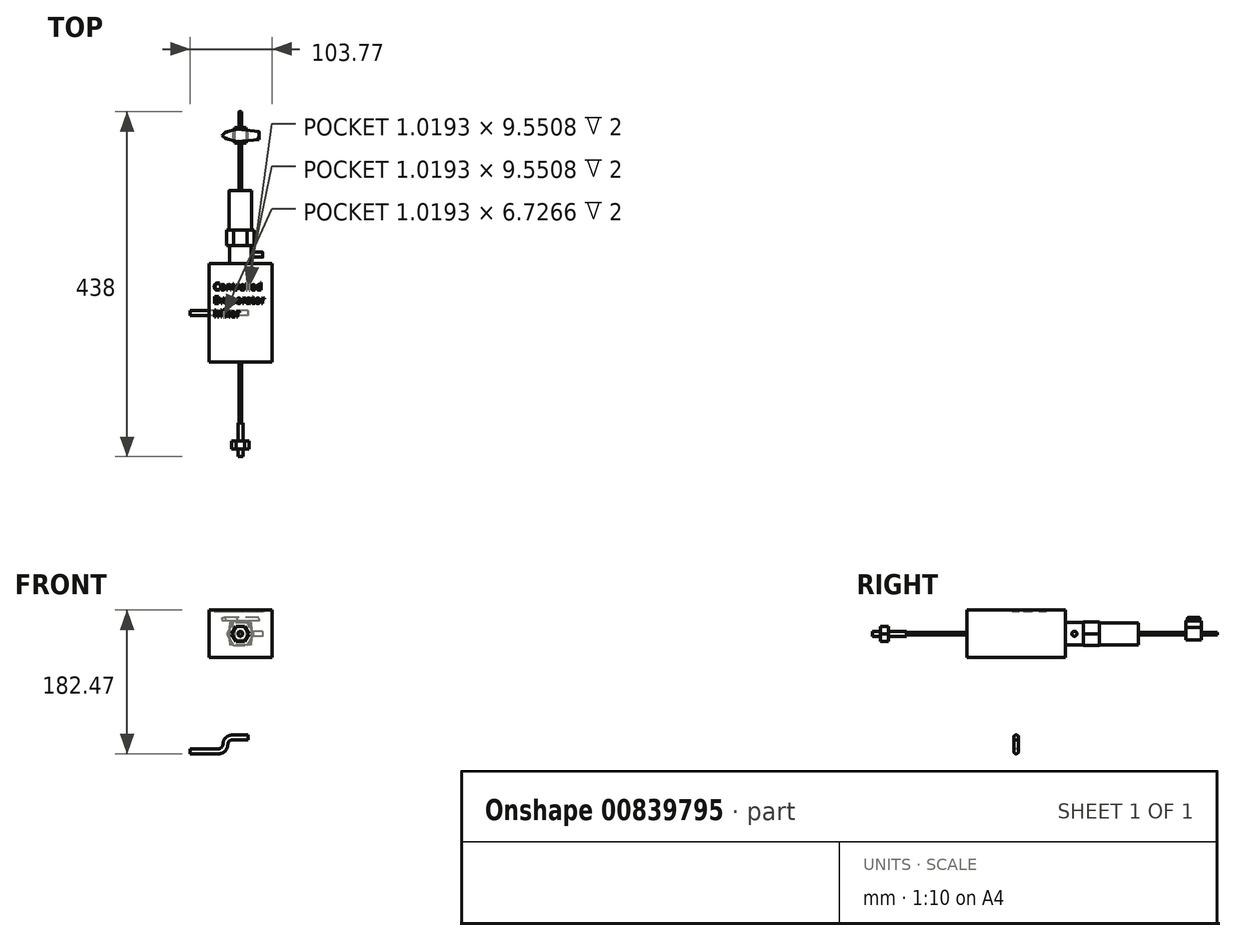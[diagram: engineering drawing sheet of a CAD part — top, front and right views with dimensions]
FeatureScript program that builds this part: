
annotation { "Feature Type Name" : "Feature", "Feature Type Description" : "" }
export const myFeature = defineFeature(function(context is Context, id is Id, definition is map)
    precondition{}
    {
        {
            var Q0;
            Q0=qCreatedBy(makeId("Top.planeOp"),FACE);
            var sketch = newSketch(context, id + "F0", { "sketchPlane" : qUnion([Q0])});
            skLineSegment(sketch, "E0.bottom", {"start": v(-40, 62.5) * mm, "end": v(40, 62.5) * mm});
            skLineSegment(sketch, "E0.top", {"start": v(-40, -62.5) * mm, "end": v(40, -62.5) * mm});
            skLineSegment(sketch, "E0.left", {"start": v(-40, 62.5) * mm, "end": v(-40, -62.5) * mm});
            skLineSegment(sketch, "E0.right", {"start": v(40, 62.5) * mm, "end": v(40, -62.5) * mm});
            skPoint(sketch, "E0.middle", {"position": v(0, 0) * mm});
            skSolve(sketch);
        }
        {
            var Q0;
            Q0 = qSketchRegion(id + "F0", true);
            extrude(context, id + "F1", {"entities" : qUnion([Q0]), "depth" : 60 * mm, "offsetDistance" : 25 * mm});
        }
        {
            var Q0;
            Q0=makeQuery(id+"F1.opExtrude","SWEPT_FACE",FACE,{"disambiguationData":[OSD([sQuery(id+"F0.wireOp",EDGE,"E0.bottom")])]});
            var sketch = newSketch(context, id + "F2", { "sketchPlane" : qUnion([Q0])});
            skLineSegment(sketch, "E1", {"start": v(-40, 30) * mm, "end": v(40, 30) * mm});
            skLineSegment(sketch, "E2.bottom", {"start": v(-13.5, 44.5) * mm, "end": v(13.5, 44.5) * mm});
            skLineSegment(sketch, "E2.top", {"start": v(-13.5, 15.5) * mm, "end": v(13.5, 15.5) * mm});
            skLineSegment(sketch, "E2.left", {"start": v(-13.5, 44.5) * mm, "end": v(-13.5, 15.5) * mm});
            skLineSegment(sketch, "E2.right", {"start": v(13.5, 44.5) * mm, "end": v(13.5, 15.5) * mm});
            skPoint(sketch, "E2.middle", {"position": v(0, 30) * mm});
            skSolve(sketch);
        }
        {
            var Q0;
            Q0 = qSketchRegion(id + "F2", true);
            extrude(context, id + "F3", {"entities" : qUnion([Q0]), "operationType" : NewBodyOperationType.ADD, "depth" : 23 * mm, "offsetDistance" : 25 * mm});
        }
        {
            var Q0;
            Q0=makeQuery(id+"F3.opExtrude","CAP_FACE",FACE,{"disambiguationData":[OSD([sQuery(id+"F2.wireOp",EDGE,"E2.bottom"),sQuery(id+"F2.wireOp",EDGE,"E2.top"),sQuery(id+"F2.wireOp",EDGE,"E2.left"),sQuery(id+"F2.wireOp",EDGE,"E2.right")])],"isStart":false});
            var sketch = newSketch(context, id + "F4", { "sketchPlane" : qUnion([Q0])});
            skLineSegment(sketch, "E3", {"start": v(-13.5, 30) * mm, "end": v(13.5, 30) * mm, "construction": true});
            skPoint(sketch, "E4.cCircle.perimeterSnap0", {"position": v(0, 44.5) * mm});
            skPoint(sketch, "E4.0.startSnap0", {"position": v(0, 44.5) * mm});
            skCircle(sketch, "E5.cCircle", {"center": v(0, 30) * mm, "radius": 15 * mm, "construction": true});
            skLineSegment(sketch, "E5.0", {"start": v(-8.66, 45) * mm, "end": v(8.66, 45) * mm});
            skLineSegment(sketch, "E5.1", {"start": v(8.66, 45) * mm, "end": v(17.32, 30) * mm});
            skLineSegment(sketch, "E5.2", {"start": v(17.32, 30) * mm, "end": v(8.66, 15) * mm});
            skLineSegment(sketch, "E5.3", {"start": v(8.66, 15) * mm, "end": v(-8.66, 15) * mm});
            skLineSegment(sketch, "E5.4", {"start": v(-8.66, 15) * mm, "end": v(-17.32, 30) * mm});
            skLineSegment(sketch, "E5.5", {"start": v(-17.32, 30) * mm, "end": v(-8.66, 45) * mm});
            skPoint(sketch, "E5.0.midPoint", {"position": v(0, 45) * mm});
            skSolve(sketch);
        }
        {
            var Q0;
            Q0 = qSketchRegion(id + "F4", true);
            extrude(context, id + "F5", {"entities" : qUnion([Q0]), "operationType" : NewBodyOperationType.ADD, "depth" : 20 * mm, "offsetDistance" : 25 * mm});
        }
        {
            var Q0;
            Q0=makeQuery(id+"F5.opExtrude","CAP_FACE",FACE,{"disambiguationData":[OSD([sQuery(id+"F4.wireOp",EDGE,"E5.0"),sQuery(id+"F4.wireOp",EDGE,"E5.1"),sQuery(id+"F4.wireOp",EDGE,"E5.2"),sQuery(id+"F4.wireOp",EDGE,"E5.3"),sQuery(id+"F4.wireOp",EDGE,"E5.4"),sQuery(id+"F4.wireOp",EDGE,"E5.5")])],"isStart":false});
            var sketch = newSketch(context, id + "F6", { "sketchPlane" : qUnion([Q0])});
            skLineSegment(sketch, "E6", {"start": v(-17.32, 30) * mm, "end": v(17.32, 30) * mm, "construction": true});
            skLineSegment(sketch, "E7.bottom", {"start": v(-14, 44) * mm, "end": v(14, 44) * mm});
            skLineSegment(sketch, "E7.top", {"start": v(-14, 16) * mm, "end": v(14, 16) * mm});
            skLineSegment(sketch, "E7.left", {"start": v(-14, 44) * mm, "end": v(-14, 16) * mm});
            skLineSegment(sketch, "E7.right", {"start": v(14, 44) * mm, "end": v(14, 16) * mm});
            skPoint(sketch, "E7.middle", {"position": v(0, 30) * mm});
            skSolve(sketch);
        }
        {
            var Q0;
            Q0 = qSketchRegion(id + "F6", true);
            extrude(context, id + "F7", {"entities" : qUnion([Q0]), "operationType" : NewBodyOperationType.ADD, "depth" : 50 * mm, "offsetDistance" : 25 * mm});
        }
        {
            var Q0;
            Q0=makeQuery(id+"F7.opExtrude","SWEPT_EDGE",EDGE,{"disambiguationData":[OSD([sQuery(id+"F6.wireOp",EDGE,"E7.bottom"),sQuery(id+"F6.wireOp",EDGE,"E7.left")])]});
            var Q1;
            Q1=makeQuery(id+"F7.opExtrude","SWEPT_EDGE",EDGE,{"disambiguationData":[OSD([sQuery(id+"F6.wireOp",EDGE,"E7.bottom"),sQuery(id+"F6.wireOp",EDGE,"E7.right")])]});
            var Q2;
            Q2=makeQuery(id+"F7.opExtrude","SWEPT_EDGE",EDGE,{"disambiguationData":[OSD([sQuery(id+"F6.wireOp",EDGE,"E7.top"),sQuery(id+"F6.wireOp",EDGE,"E7.right")])]});
            var Q3;
            Q3=makeQuery(id+"F7.opExtrude","SWEPT_EDGE",EDGE,{"disambiguationData":[OSD([sQuery(id+"F6.wireOp",EDGE,"E7.top"),sQuery(id+"F6.wireOp",EDGE,"E7.left")])]});
            fillet(context, id + "F8", {"entities" : qUnion([Q0, Q1, Q2, Q3]), "radius" : 5 * mm, "tangentPropagation" : true, "allowEdgeOverflow" : false});
        }
        {
            var Q0;
            Q0=makeQuery(id+"F7.opExtrude","CAP_FACE",FACE,{"disambiguationData":[OSD([sQuery(id+"F6.wireOp",EDGE,"E7.bottom"),sQuery(id+"F6.wireOp",EDGE,"E7.top"),sQuery(id+"F6.wireOp",EDGE,"E7.left"),sQuery(id+"F6.wireOp",EDGE,"E7.right")])],"isStart":false});
            var sketch = newSketch(context, id + "F9", { "sketchPlane" : qUnion([Q0])});
            skLineSegment(sketch, "E8", {"start": v(-14, 30) * mm, "end": v(14, 30) * mm, "construction": true});
            skCircle(sketch, "E9", {"center": v(0, 30) * mm, "radius": 1.59 * mm});
            skSolve(sketch);
        }
        {
            var Q0;
            Q0 = qSketchRegion(id + "F9", true);
            extrude(context, id + "F10", {"entities" : qUnion([Q0]), "operationType" : NewBodyOperationType.ADD, "depth" : 60 * mm, "offsetDistance" : 25 * mm});
        }
        {
            var Q0;
            Q0=makeQuery(id+"F10.opExtrude","CAP_FACE",FACE,{"disambiguationData":[OSD([sQuery(id+"F9.wireOp",EDGE,"E9")])],"isStart":false});
            var sketch = newSketch(context, id + "F11", { "sketchPlane" : qUnion([Q0])});
            skLineSegment(sketch, "E10.bottom", {"start": v(-7.5, 38) * mm, "end": v(7.5, 38) * mm});
            skLineSegment(sketch, "E10.top", {"start": v(-7.5, 22) * mm, "end": v(7.5, 22) * mm});
            skLineSegment(sketch, "E10.left", {"start": v(-7.5, 38) * mm, "end": v(-7.5, 22) * mm});
            skLineSegment(sketch, "E10.right", {"start": v(7.5, 38) * mm, "end": v(7.5, 22) * mm});
            skPoint(sketch, "E10.middle", {"position": v(0, 30) * mm});
            skSolve(sketch);
        }
        {
            var Q0;
            Q0 = qSketchRegion(id + "F11", true);
            extrude(context, id + "F12", {"entities" : qUnion([Q0]), "operationType" : NewBodyOperationType.ADD, "depth" : 20 * mm, "offsetDistance" : 25 * mm});
        }
        {
            var Q0;
            Q0=makeQuery(id+"F12.opExtrude","CAP_FACE",FACE,{"disambiguationData":[OSD([sQuery(id+"F11.wireOp",EDGE,"E10.bottom"),sQuery(id+"F11.wireOp",EDGE,"E10.top"),sQuery(id+"F11.wireOp",EDGE,"E10.left"),sQuery(id+"F11.wireOp",EDGE,"E10.right")])],"isStart":false});
            var sketch = newSketch(context, id + "F13", { "sketchPlane" : qUnion([Q0])});
            skLineSegment(sketch, "E11", {"start": v(-7.5, 30) * mm, "end": v(7.5, 30) * mm, "construction": true});
            skCircle(sketch, "E12", {"center": v(0, 30) * mm, "radius": 1.59 * mm});
            skSolve(sketch);
        }
        {
            var Q0;
            Q0=makeQuery(id+"F13.imprint","IMPRINT",FACE,{"disambiguationData":[TD([[makeQuery(id+"F13.imprint","IMPRINT",EDGE,{"derivedFrom":sQuery(id+"F13.wireOp",EDGE,"E12")}),1.0]])]});
            var Q1;
            Q1 = qConstructionFilter(qBodyType(qCreatedBy(id + "F13" ,EDGE), BodyType.WIRE), ConstructionObject.NO);
            extrude(context, id + "F14", {"entities" : qUnion([Q0]), "operationType" : NewBodyOperationType.ADD, "surfaceEntities" : qUnion([Q1]), "depth" : 20 * mm, "offsetDistance" : 25 * mm});
        }
        {
            var Q0;
            Q0=makeQuery(id+"F12.opExtrude","SWEPT_FACE",FACE,{"disambiguationData":[OSD([sQuery(id+"F11.wireOp",EDGE,"E10.bottom")])]});
            var sketch = newSketch(context, id + "F15", { "sketchPlane" : qUnion([Q0])});
            skLineSegment(sketch, "E13", {"start": v(-7.5, 225.5) * mm, "end": v(7.5, 225.5) * mm, "construction": true});
            skCircle(sketch, "E14", {"center": v(0, 225.5) * mm, "radius": 10 * mm});
            skSolve(sketch);
        }
        {
            var Q0;
            Q0 = qSketchRegion(id + "F15", true);
            extrude(context, id + "F16", {"entities" : qUnion([Q0]), "operationType" : NewBodyOperationType.ADD, "depth" : 8 * mm, "offsetDistance" : 25 * mm});
        }
        {
            var Q0;
            Q0=makeQuery(id+"F16.opExtrude","CAP_FACE",FACE,{"disambiguationData":[OSD([sQuery(id+"F15.wireOp",EDGE,"E14")])],"isStart":false});
            var sketch = newSketch(context, id + "F17", { "sketchPlane" : qUnion([Q0])});
            skLineSegment(sketch, "E15.bottom", {"start": v(-23.5, 233.5) * mm, "end": v(23.5, 233.5) * mm, "construction": true});
            skLineSegment(sketch, "E15.top", {"start": v(-23.5, 217.5) * mm, "end": v(23.5, 217.5) * mm, "construction": true});
            skLineSegment(sketch, "E15.left", {"start": v(-23.5, 233.5) * mm, "end": v(-23.5, 217.5) * mm, "construction": true});
            skLineSegment(sketch, "E15.right", {"start": v(23.5, 233.5) * mm, "end": v(23.5, 217.5) * mm, "construction": true});
            skPoint(sketch, "E15.middle", {"position": v(0, 225.5) * mm});
            skPoint(sketch, "E16", {"position": v(23.5, 230.5) * mm});
            skPoint(sketch, "E17", {"position": v(23.5, 220.5) * mm});
            skLineSegment(sketch, "E18", {"start": v(23.5, 230.5) * mm, "end": v(-4.34, 233.5) * mm});
            skLineSegment(sketch, "E19", {"start": v(-4.34, 233.5) * mm, "end": v(-18.8, 229.5) * mm});
            skLineSegment(sketch, "E20", {"start": v(-18.8, 229.5) * mm, "end": v(-23.5, 225.5) * mm});
            skLineSegment(sketch, "E21", {"start": v(-23.5, 225.5) * mm, "end": v(23.5, 225.5) * mm, "construction": true});
            skLineSegment(sketch, "E22.MirrorCS", {"start": v(-18.8, 221.5) * mm, "end": v(-23.5, 225.5) * mm});
            skLineSegment(sketch, "E23.MirrorCS", {"start": v(-4.34, 217.5) * mm, "end": v(-18.8, 221.5) * mm});
            skLineSegment(sketch, "E24.MirrorCS", {"start": v(23.5, 220.5) * mm, "end": v(-4.34, 217.5) * mm});
            skLineSegment(sketch, "E25", {"start": v(23.5, 230.5) * mm, "end": v(23.5, 220.5) * mm});
            skSolve(sketch);
        }
        {
            var Q0;
            {var subQ4=sQuery(id+"F17.wireOp",EDGE,"E20");Q0=makeQuery(id+"F17.imprint","IMPRINT",FACE,{"disambiguationData":[TD([[makeQuery(id+"F17.imprint","IMPRINT",EDGE,{"derivedFrom":subQ4}),1.0]])]});}
            var Q1;
            {var subQ5=sQuery(id+"F17.wireOp",EDGE,"E19");var subQ6=sQuery(id+"F17.wireOp",EDGE,"E18");var subQ7=makeQuery(id+"F17.imprint","INTERSECT",VERTEX,{"derivedFrom":[subQ6,subQ5]});Q1=makeQuery(id+"F17.imprint","IMPRINT",FACE,{"disambiguationData":[TD([[makeQuery(id+"F17.imprint","IMPRINT",EDGE,{"disambiguationData":[TD([[subQ7,1.0]])],"derivedFrom":subQ6}),1.0]])]});}
            var Q2;
            {var subQ0=sQuery(id+"F17.wireOp",EDGE,"E25");Q2=makeQuery(id+"F17.imprint","IMPRINT",FACE,{"disambiguationData":[TD([[makeQuery(id+"F17.imprint","IMPRINT",EDGE,{"derivedFrom":subQ0}),-1.0]])]});}
            extrude(context, id + "F18", {"entities" : qUnion([Q0, Q1, Q2]), "operationType" : NewBodyOperationType.ADD, "depth" : 5 * mm, "offsetDistance" : 25 * mm});
        }
        {
            var Q0;
            Q0=makeQuery(id+"F18.opExtrude","CAP_EDGE",EDGE,{"disambiguationData":[OSD([sQuery(id+"F17.wireOp",EDGE,"E18")])],"isStart":false});
            var Q1;
            Q1=makeQuery(id+"F18.opExtrude","CAP_EDGE",EDGE,{"disambiguationData":[OSD([sQuery(id+"F17.wireOp",EDGE,"E19")])],"isStart":false});
            var Q2;
            Q2=makeQuery(id+"F18.opExtrude","CAP_EDGE",EDGE,{"disambiguationData":[OSD([sQuery(id+"F17.wireOp",EDGE,"E20")])],"isStart":false});
            var Q3;
            Q3=makeQuery(id+"F18.opExtrude","CAP_EDGE",EDGE,{"disambiguationData":[OSD([sQuery(id+"F17.wireOp",EDGE,"E22.MirrorCS")])],"isStart":false});
            var Q4;
            Q4=makeQuery(id+"F18.opExtrude","CAP_EDGE",EDGE,{"disambiguationData":[OSD([sQuery(id+"F17.wireOp",EDGE,"E23.MirrorCS")])],"isStart":false});
            var Q5;
            Q5=makeQuery(id+"F18.opExtrude","CAP_EDGE",EDGE,{"disambiguationData":[OSD([sQuery(id+"F17.wireOp",EDGE,"E24.MirrorCS")])],"isStart":false});
            var Q6;
            Q6=makeQuery(id+"F18.opExtrude","CAP_EDGE",EDGE,{"disambiguationData":[OSD([sQuery(id+"F17.wireOp",EDGE,"E25")])],"isStart":false});
            fillet(context, id + "F19", {"entities" : qUnion([Q0, Q1, Q2, Q3, Q4, Q5, Q6]), "radius" : 2 * mm, "tangentPropagation" : true, "allowEdgeOverflow" : false});
        }
        {
            var Q0;
            Q0=makeQuery(id+"F1.opExtrude","SWEPT_FACE",FACE,{"disambiguationData":[OSD([sQuery(id+"F0.wireOp",EDGE,"E0.top")])]});
            var sketch = newSketch(context, id + "F20", { "sketchPlane" : qUnion([Q0])});
            skLineSegment(sketch, "E26", {"start": v(-40, 30) * mm, "end": v(40, 30) * mm, "construction": true});
            skCircle(sketch, "E27", {"center": v(0, 30) * mm, "radius": 1.59 * mm});
            skPoint(sketch, "E28", {"position": v(0, 31.59) * mm});
            skSolve(sketch);
        }
        {
            var Q0;
            Q0 = qSketchRegion(id + "F20", true);
            extrude(context, id + "F21", {"entities" : qUnion([Q0]), "operationType" : NewBodyOperationType.ADD, "depth" : 77 * mm, "offsetDistance" : 25 * mm});
        }
        {
            var Q0;
            Q0=makeQuery(id+"F21.opExtrude","CAP_FACE",FACE,{"disambiguationData":[OSD([sQuery(id+"F20.wireOp",EDGE,"E27")])],"isStart":false});
            var sketch = newSketch(context, id + "F22", { "sketchPlane" : qUnion([Q0])});
            skCircle(sketch, "E29", {"center": v(0, 30) * mm, "radius": 3.18 * mm});
            skSolve(sketch);
        }
        {
            var Q0;
            Q0 = qSketchRegion(id + "F22", true);
            extrude(context, id + "F23", {"entities" : qUnion([Q0]), "operationType" : NewBodyOperationType.ADD, "depth" : 23 * mm, "offsetDistance" : 25 * mm});
        }
        {
            var Q0;
            Q0=makeQuery(id+"F23.opExtrude","CAP_FACE",FACE,{"disambiguationData":[OSD([sQuery(id+"F22.wireOp",EDGE,"E29")])],"isStart":false});
            var sketch = newSketch(context, id + "F24", { "sketchPlane" : qUnion([Q0])});
            skCircle(sketch, "E30.cCircle", {"center": v(0, 30) * mm, "radius": 9.5 * mm, "construction": true});
            skLineSegment(sketch, "E30.0", {"start": v(-5.48, 39.5) * mm, "end": v(5.48, 39.5) * mm});
            skLineSegment(sketch, "E30.1", {"start": v(5.48, 39.5) * mm, "end": v(10.97, 30) * mm});
            skLineSegment(sketch, "E30.2", {"start": v(10.97, 30) * mm, "end": v(5.48, 20.5) * mm});
            skLineSegment(sketch, "E30.3", {"start": v(5.48, 20.5) * mm, "end": v(-5.48, 20.5) * mm});
            skLineSegment(sketch, "E30.4", {"start": v(-5.48, 20.5) * mm, "end": v(-10.97, 30) * mm});
            skLineSegment(sketch, "E30.5", {"start": v(-10.97, 30) * mm, "end": v(-5.48, 39.5) * mm});
            skPoint(sketch, "E30.0.midPoint", {"position": v(0, 39.5) * mm});
            skSolve(sketch);
        }
        {
            var Q0;
            Q0 = qSketchRegion(id + "F24", true);
            extrude(context, id + "F25", {"entities" : qUnion([Q0]), "operationType" : NewBodyOperationType.ADD, "depth" : 10 * mm, "offsetDistance" : 25 * mm});
        }
        {
            var Q0;
            Q0=makeQuery(id+"F25.opExtrude","CAP_FACE",FACE,{"disambiguationData":[OSD([sQuery(id+"F24.wireOp",EDGE,"E30.0"),sQuery(id+"F24.wireOp",EDGE,"E30.1"),sQuery(id+"F24.wireOp",EDGE,"E30.2"),sQuery(id+"F24.wireOp",EDGE,"E30.3"),sQuery(id+"F24.wireOp",EDGE,"E30.4"),sQuery(id+"F24.wireOp",EDGE,"E30.5")])],"isStart":false});
            var sketch = newSketch(context, id + "F26", { "sketchPlane" : qUnion([Q0])});
            skCircle(sketch, "E31", {"center": v(0, 30) * mm, "radius": 3.17 * mm});
            skLineSegment(sketch, "E32", {"start": v(-10.97, 30) * mm, "end": v(10.97, 30) * mm, "construction": true});
            skSolve(sketch);
        }
        {
            var Q0;
            Q0 = qSketchRegion(id + "F26", true);
            extrude(context, id + "F27", {"entities" : qUnion([Q0]), "operationType" : NewBodyOperationType.ADD, "depth" : 10 * mm, "offsetDistance" : 25 * mm});
        }
        {
            var Q0;
            Q0=makeQuery(id+"F1.opExtrude","CAP_FACE",FACE,{"disambiguationData":[OSD([sQuery(id+"F0.wireOp",EDGE,"E0.bottom"),sQuery(id+"F0.wireOp",EDGE,"E0.top"),sQuery(id+"F0.wireOp",EDGE,"E0.left"),sQuery(id+"F0.wireOp",EDGE,"E0.right")])],"isStart":false});
            var sketch = newSketch(context, id + "F28", { "sketchPlane" : qUnion([Q0])});
            skText(sketch, "E33", { "text": "Controlled\nEvaporator\nMixer", "fontName": "OpenSans-Regular.ttf"});
            const initialGuessF28  = {"E33": [-0.03383, 0.02904, 1, 0, 0.00905]};
            skSetInitialGuess(sketch, initialGuessF28);
            skSolve(sketch);
        }
        {
            var Q0;
            Q0 = qSketchRegion(id + "F28", true);
            extrude(context, id + "F29", {"entities" : qUnion([Q0]), "operationType" : NewBodyOperationType.REMOVE, "oppositeDirection" : true, "depth" : 2 * mm, "offsetDistance" : 25 * mm});
        }
        {
            var Q0;
            Q0=makeQuery(id+"F3.opExtrude","SWEPT_FACE",FACE,{"disambiguationData":[OSD([sQuery(id+"F2.wireOp",EDGE,"E2.left")])]});
            var sketch = newSketch(context, id + "F30", { "sketchPlane" : qUnion([Q0])});
            skLineSegment(sketch, "E34", {"start": v(74, 44.5) * mm, "end": v(74, 15.5) * mm, "construction": true});
            skCircle(sketch, "E35", {"center": v(74, 30) * mm, "radius": 3.17 * mm});
            skSolve(sketch);
        }
        {
            var Q0;
            Q0=makeQuery(id+"F30.imprint","IMPRINT",FACE,{"disambiguationData":[TD([[makeQuery(id+"F30.imprint","IMPRINT",EDGE,{"derivedFrom":sQuery(id+"F30.wireOp",EDGE,"E35")}),1.0]])]});
            extrude(context, id + "F31", {"entities" : qUnion([Q0]), "operationType" : NewBodyOperationType.ADD, "depth" : 15 * mm, "offsetDistance" : 25 * mm});
        }
        {
            var Q0;
            Q0=qCreatedBy(makeId("Front.planeOp"),FACE);
            var sketch = newSketch(context, id + "F32", { "sketchPlane" : qUnion([Q0])});
            skLineSegment(sketch, "E36", {"start": v(9.73, -101.8) * mm, "end": v(-10.27, -101.8) * mm});
            skLineSegment(sketch, "E37", {"start": v(-10.27, -101.8) * mm, "end": v(-10.27, -110.55) * mm, "construction": true});
            skArc(sketch, "E38", {"start": v(-10.27, -101.8) * mm, "mid": v(-16.46, -104.36) * mm, "end": v(-19.02, -110.55) * mm});
            skLineSegment(sketch, "E39", {"start": v(-10.27, -110.55) * mm, "end": v(-27.77, -110.55) * mm, "construction": true});
            skArc(sketch, "E40", {"start": v(-19.02, -110.55) * mm, "mid": v(-21.59, -116.74) * mm, "end": v(-27.77, -119.3) * mm});
            skLineSegment(sketch, "E41", {"start": v(-27.77, -119.3) * mm, "end": v(-63.77, -119.3) * mm});
            skSolve(sketch);
        }
        {
            var Q0;
            Q0=sQuery(id+"F32.wireOp",VERTEX,"E36.start");
            var Q1;
            Q1=sQuery(id+"F32.wireOp",EDGE,"E36");
            cPlane(context, id + "F33", {"entities" : qUnion([Q0, Q1]), "cplaneType" : CPlaneType.CURVE_POINT, "offset" : 25 * mm, "width" : 150 * mm, "height" : 150 * mm});
        }
        {
            var Q0;
            Q0=qCreatedBy(id+"F33.planeOp",FACE);
            var sketch = newSketch(context, id + "F34", { "sketchPlane" : qUnion([Q0])});
            skCircle(sketch, "E42", {"center": v(0, -101.8) * mm, "radius": 3.18 * mm});
            skSolve(sketch);
        }
        {
            var Q0;
            Q0=makeQuery(id+"F34.imprint","IMPRINT",FACE,{"disambiguationData":[TD([[makeQuery(id+"F34.imprint","IMPRINT",EDGE,{"derivedFrom":sQuery(id+"F34.wireOp",EDGE,"E42")}),1.0]])]});
            var Q1;
            Q1=sQuery(id+"F32.wireOp",EDGE,"E36");
            var Q2;
            Q2=sQuery(id+"F32.wireOp",EDGE,"E38");
            var Q3;
            Q3=sQuery(id+"F32.wireOp",EDGE,"E40");
            var Q4;
            Q4=sQuery(id+"F32.wireOp",EDGE,"E41");
            sweep(context, id + "F35", {"profiles" : qUnion([Q0]), "path" : qUnion([Q1, Q2, Q3, Q4])});
        }
    });
